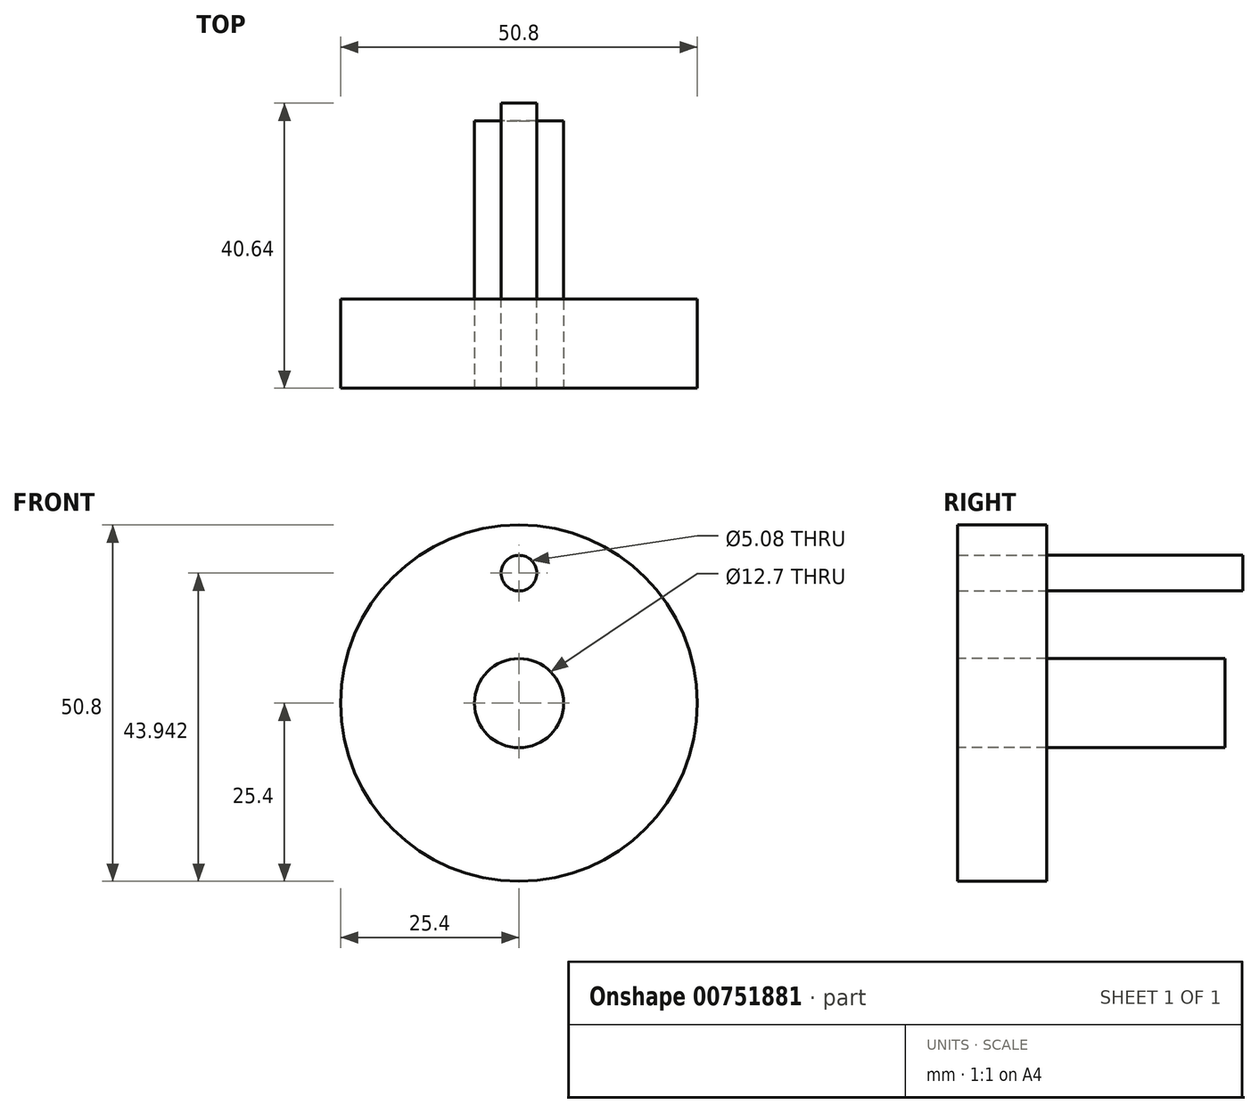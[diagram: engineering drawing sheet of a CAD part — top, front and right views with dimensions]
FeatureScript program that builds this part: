
annotation { "Feature Type Name" : "Feature", "Feature Type Description" : "" }
export const myFeature = defineFeature(function(context is Context, id is Id, definition is map)
    precondition{}
    {
        {
            var Q0;
            Q0=qCreatedBy(makeId("Front.planeOp"),FACE);
            var sketch = newSketch(context, id + "F0", { "sketchPlane" : qUnion([Q0])});
            skCircle(sketch, "E0", {"center": v(0, 0) * mm, "radius": 25.4 * mm});
            skCircle(sketch, "E1", {"center": v(0, 18.54) * mm, "radius": 2.54 * mm});
            skCircle(sketch, "E2", {"center": v(0, 0) * mm, "radius": 6.35 * mm});
            skSolve(sketch);
        }
        {
            var Q0;
            Q0=makeQuery(id+"F0.imprint","IMPRINT",FACE,{"disambiguationData":[TD([[makeQuery(id+"F0.imprint","IMPRINT",EDGE,{"derivedFrom":sQuery(id+"F0.wireOp",EDGE,"E0")}),1.0]])]});
            extrude(context, id + "F1", {"entities" : qUnion([Q0]), "depth" : 12.7 * mm, "offsetDistance" : 25.4 * mm});
        }
        {
            var Q0;
            Q0=makeQuery(id+"F1.opExtrude","CAP_FACE",FACE,{"disambiguationData":[OSD([sQuery(id+"F0.wireOp",EDGE,"E0"),sQuery(id+"F0.wireOp",EDGE,"E1"),sQuery(id+"F0.wireOp",EDGE,"E2")])],"isStart":false});
            var sketch = newSketch(context, id + "F2", { "sketchPlane" : qUnion([Q0])});
            skCircle(sketch, "E3", {"center": v(0, 0) * mm, "radius": 6.35 * mm});
            skSolve(sketch);
        }
        {
            var Q0;
            Q0=makeQuery(id+"F2.imprint","IMPRINT",FACE,{"disambiguationData":[TD([[makeQuery(id+"F2.imprint","IMPRINT",EDGE,{"derivedFrom":sQuery(id+"F2.wireOp",EDGE,"E3")}),1.0]])]});
            extrude(context, id + "F3", {"entities" : qUnion([Q0]), "oppositeDirection" : true, "depth" : 38.1 * mm, "offsetDistance" : 25.4 * mm});
        }
        {
            var Q0;
            Q0=makeQuery(id+"F1.opExtrude","CAP_FACE",FACE,{"disambiguationData":[OSD([sQuery(id+"F0.wireOp",EDGE,"E0"),sQuery(id+"F0.wireOp",EDGE,"E1"),sQuery(id+"F0.wireOp",EDGE,"E2")])],"isStart":false});
            var sketch = newSketch(context, id + "F4", { "sketchPlane" : qUnion([Q0])});
            skCircle(sketch, "E4", {"center": v(0, 18.54) * mm, "radius": 2.54 * mm});
            skSolve(sketch);
        }
        {
            var Q0;
            Q0=makeQuery(id+"F1.opExtrude","CAP_FACE",FACE,{"disambiguationData":[OSD([sQuery(id+"F0.wireOp",EDGE,"E0"),sQuery(id+"F0.wireOp",EDGE,"E1"),sQuery(id+"F0.wireOp",EDGE,"E2")])],"isStart":true});
            var sketch = newSketch(context, id + "F5", { "sketchPlane" : qUnion([Q0])});
            skCircle(sketch, "E5", {"center": v(0, 18.54) * mm, "radius": 2.54 * mm});
            skSolve(sketch);
        }
        {
            var Q0;
            Q0=makeQuery(id+"F5.imprint","IMPRINT",FACE,{"disambiguationData":[TD([[makeQuery(id+"F5.imprint","IMPRINT",EDGE,{"derivedFrom":sQuery(id+"F5.wireOp",EDGE,"E5")}),-1.0]])]});
            extrude(context, id + "F6", {"entities" : qUnion([Q0]), "depth" : 27.94 * mm, "offsetDistance" : 25.4 * mm});
        }
    });
